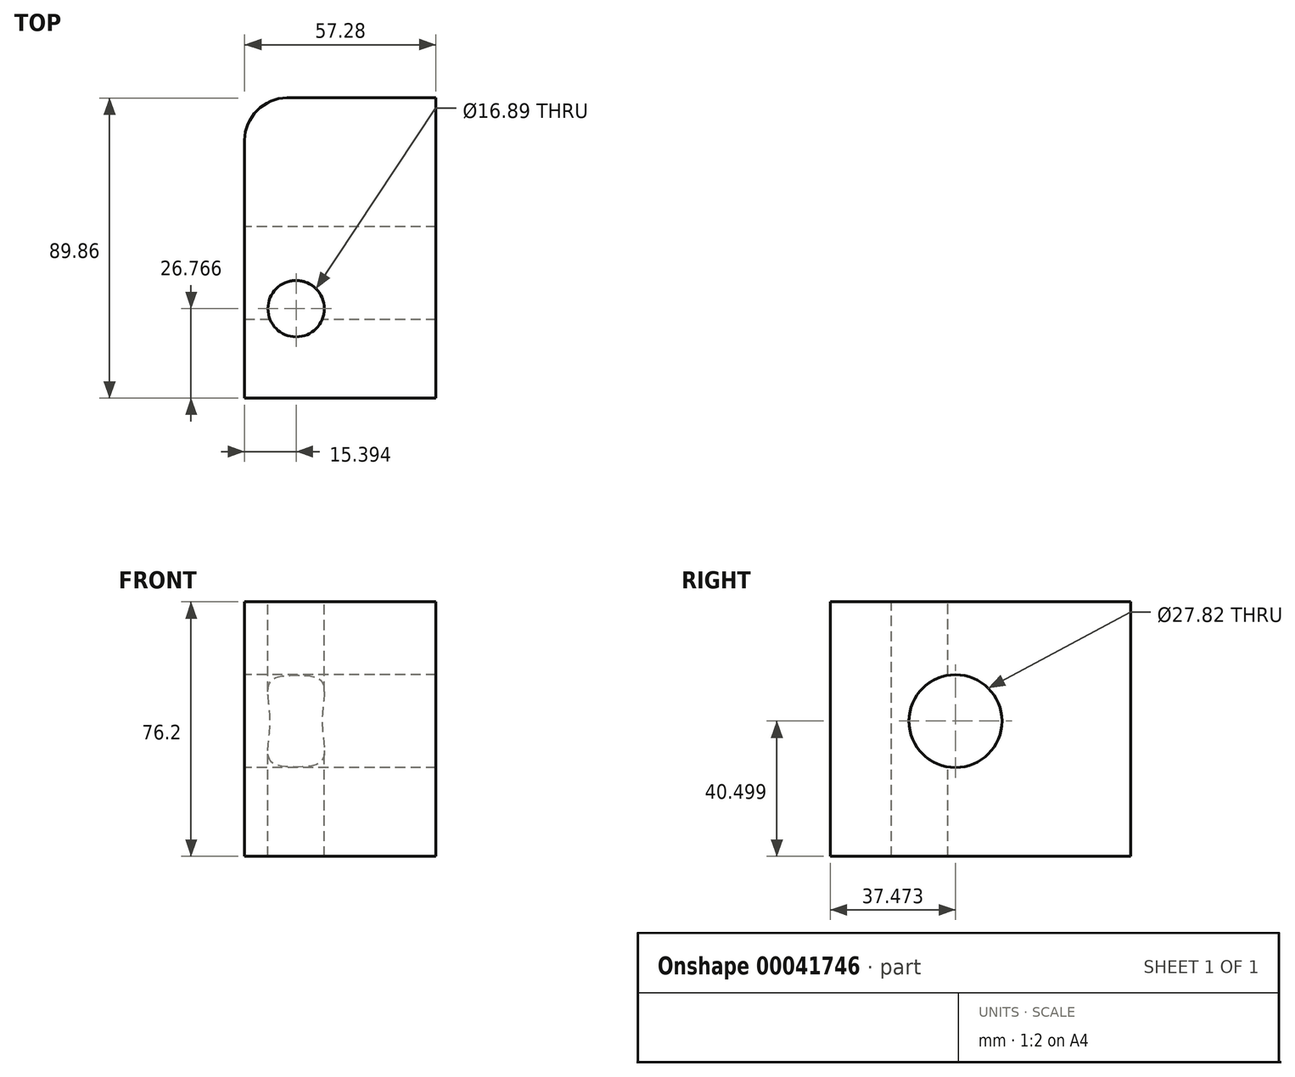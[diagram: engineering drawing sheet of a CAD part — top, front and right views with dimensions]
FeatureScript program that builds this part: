
annotation { "Feature Type Name" : "Feature", "Feature Type Description" : "" }
export const myFeature = defineFeature(function(context is Context, id is Id, definition is map)
    precondition{}
    {
        {
            var Q0;
            Q0=qCreatedBy(makeId("Top.planeOp"),FACE);
            var sketch = newSketch(context, id + "F0", { "sketchPlane" : qUnion([Q0])});
            skLineSegment(sketch, "E0.rect.bottom", {"start": v(-28.64, -44.93) * mm, "end": v(28.64, -44.93) * mm});
            skLineSegment(sketch, "E0.rect.top", {"start": v(-15.94, 44.93) * mm, "end": v(28.64, 44.93) * mm});
            skLineSegment(sketch, "E0.rect.left", {"start": v(-28.64, -44.93) * mm, "end": v(-28.64, 32.23) * mm});
            skLineSegment(sketch, "E0.rect.right", {"start": v(28.64, -44.93) * mm, "end": v(28.64, 44.93) * mm});
            skPoint(sketch, "E0.rect.middle", {"position": v(0, 0) * mm});
            skPoint(sketch, "E1.visualSharp", {"position": v(-28.64, 44.93) * mm});
            skArc(sketch, "E1.filletArc", {"start": v(-15.94, 44.93) * mm, "mid": v(-24.92, 41.21) * mm, "end": v(-28.64, 32.23) * mm});
            skSolve(sketch);
        }
        {
            var Q0;
            Q0=makeQuery(id+"F0.imprint","IMPRINT",FACE,{"disambiguationData":[TD([[makeQuery(id+"F0.imprint","IMPRINT",EDGE,{"derivedFrom":sQuery(id+"F0.wireOp",EDGE,"E0.rect.bottom")}),1.0]])]});
            extrude(context, id + "F1", {"entities" : qUnion([Q0]), "depth" : 76.2 * mm});
        }
        {
            var Q0;
            Q0=makeQuery(id+"F1.opExtrude","CAP_FACE",FACE,{"disambiguationData":[OSD([sQuery(id+"F0.wireOp",EDGE,"E0.rect.bottom"),sQuery(id+"F0.wireOp",EDGE,"E0.rect.top"),sQuery(id+"F0.wireOp",EDGE,"E0.rect.left"),sQuery(id+"F0.wireOp",EDGE,"E0.rect.right"),sQuery(id+"F0.wireOp",EDGE,"E1.filletArc")])],"isStart":false});
            var sketch = newSketch(context, id + "F2", { "sketchPlane" : qUnion([Q0])});
            skCircle(sketch, "E2", {"center": v(-13.25, -18.16) * mm, "radius": 8.44 * mm});
            skSolve(sketch);
        }
        {
            var Q0;
            Q0 = qSketchRegion(id + "F2", true);
            extrude(context, id + "F3", {"entities" : qUnion([Q0]), "operationType" : NewBodyOperationType.REMOVE, "endBound" : BoundingType.THROUGH_ALL, "oppositeDirection" : true, "depth" : 25.4 * mm});
        }
        {
            var Q0;
            Q0=makeQuery(id+"F1.opExtrude","SWEPT_FACE",FACE,{"disambiguationData":[OSD([sQuery(id+"F0.wireOp",EDGE,"E0.rect.left")])]});
            var sketch = newSketch(context, id + "F4", { "sketchPlane" : qUnion([Q0])});
            skCircle(sketch, "E3", {"center": v(7.46, 40.5) * mm, "radius": 13.9 * mm});
            skSolve(sketch);
        }
        {
            var Q0;
            Q0 = qSketchRegion(id + "F4", true);
            extrude(context, id + "F5", {"entities" : qUnion([Q0]), "operationType" : NewBodyOperationType.REMOVE, "endBound" : BoundingType.THROUGH_ALL, "oppositeDirection" : true, "depth" : 25.4 * mm});
        }
    });
